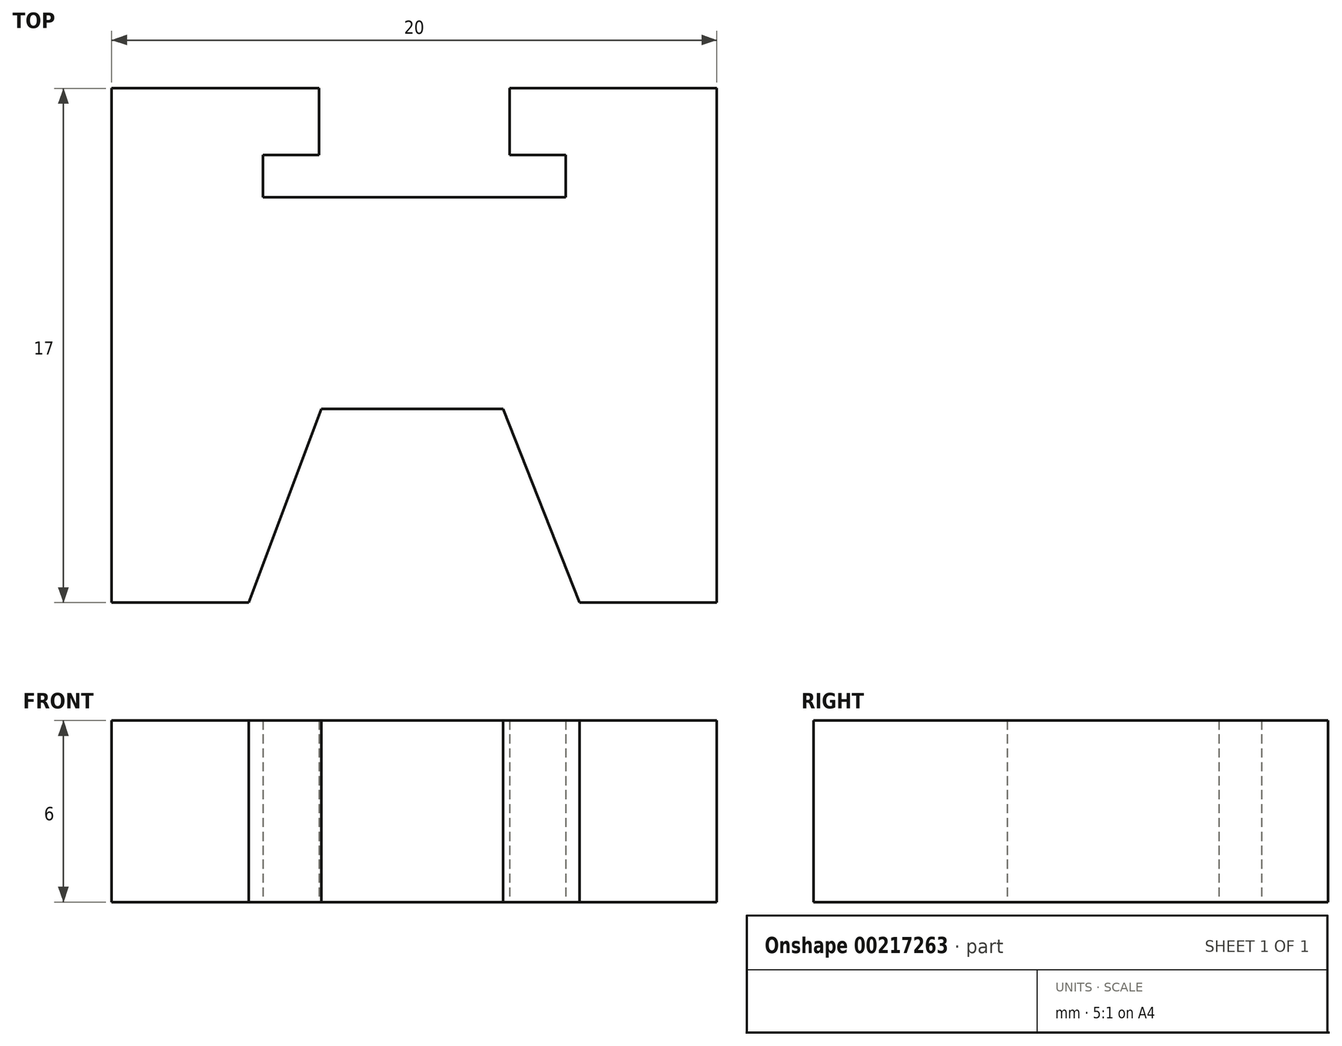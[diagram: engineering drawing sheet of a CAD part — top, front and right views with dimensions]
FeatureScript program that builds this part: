
annotation { "Feature Type Name" : "Feature", "Feature Type Description" : "" }
export const myFeature = defineFeature(function(context is Context, id is Id, definition is map)
    precondition{}
    {
        {
            var Q0;
            Q0=qCreatedBy(makeId("Top.planeOp"),FACE);
            var sketch = newSketch(context, id + "F0", { "sketchPlane" : qUnion([Q0])});
            skLineSegment(sketch, "E0.bottom", {"start": v(5, 5.81) * mm, "end": v(-5, 5.81) * mm});
            skPoint(sketch, "E0.middle", {"position": v(0, -7.59) * mm});
            skLineSegment(sketch, "E1", {"start": v(-10, 9.41) * mm, "end": v(-3.15, 9.41) * mm});
            skLineSegment(sketch, "E2", {"start": v(-3.15, 9.41) * mm, "end": v(-3.15, 7.21) * mm});
            skLineSegment(sketch, "E3", {"start": v(-3.15, 7.21) * mm, "end": v(-5, 7.21) * mm});
            skLineSegment(sketch, "E4", {"start": v(-5, 7.21) * mm, "end": v(-5, 5.81) * mm});
            skLineSegment(sketch, "E5", {"start": v(10, 9.41) * mm, "end": v(3.15, 9.41) * mm});
            skLineSegment(sketch, "E6", {"start": v(3.15, 9.41) * mm, "end": v(3.15, 7.21) * mm});
            skLineSegment(sketch, "E7", {"start": v(3.15, 7.21) * mm, "end": v(5, 7.21) * mm});
            skLineSegment(sketch, "E8", {"start": v(5, 7.21) * mm, "end": v(5, 5.81) * mm});
            skLineSegment(sketch, "E9", {"start": v(-5.47, -7.59) * mm, "end": v(-3.07, -1.19) * mm});
            skLineSegment(sketch, "E10", {"start": v(-3.07, -1.19) * mm, "end": v(2.93, -1.19) * mm});
            skLineSegment(sketch, "E11", {"start": v(2.93, -1.19) * mm, "end": v(5.46, -7.59) * mm});
            skPoint(sketch, "E12", {"position": v(-0.07, -1.19) * mm});
            skLineSegment(sketch, "E13", {"start": v(-5.47, -7.59) * mm, "end": v(-10, -7.59) * mm});
            skLineSegment(sketch, "E14", {"start": v(5.46, -7.59) * mm, "end": v(10, -7.59) * mm});
            skPoint(sketch, "E0.top.end.orphan", {"position": v(-19.87, -20.99) * mm});
            skPoint(sketch, "E15.orphan", {"position": v(20.16, -20.99) * mm});
            skPoint(sketch, "E16", {"position": v(-10, 9.41) * mm});
            skPoint(sketch, "E17", {"position": v(10, 9.41) * mm});
            skLineSegment(sketch, "E18", {"start": v(-10, 9.41) * mm, "end": v(-10, -7.59) * mm});
            skLineSegment(sketch, "E19", {"start": v(10, 9.41) * mm, "end": v(10, -7.59) * mm});
            skPoint(sketch, "E20.end.orphan", {"position": v(-20, 9.41) * mm});
            skPoint(sketch, "E0.right.start.orphan", {"position": v(-20.15, 5.81) * mm});
            skPoint(sketch, "E21.orphan", {"position": v(-20.01, -7.59) * mm});
            skPoint(sketch, "E22.end.orphan", {"position": v(20, 9.41) * mm});
            skPoint(sketch, "E0.left.end.orphan", {"position": v(20.02, -7.59) * mm});
            skPoint(sketch, "E0.left.start.orphan", {"position": v(19.87, 5.81) * mm});
            skPoint(sketch, "E23.start.orphan", {"position": v(-0.14, 5.81) * mm});
            skSolve(sketch);
        }
        {
            var Q0;
            Q0=makeQuery(id+"F0.imprint","IMPRINT",FACE,{"disambiguationData":[TD([[makeQuery(id+"F0.imprint","IMPRINT",EDGE,{"derivedFrom":sQuery(id+"F0.wireOp",EDGE,"E0.bottom")}),1.0]])]});
            extrude(context, id + "F1", {"entities" : qUnion([Q0]), "depth" : 6 * mm});
        }
    });
